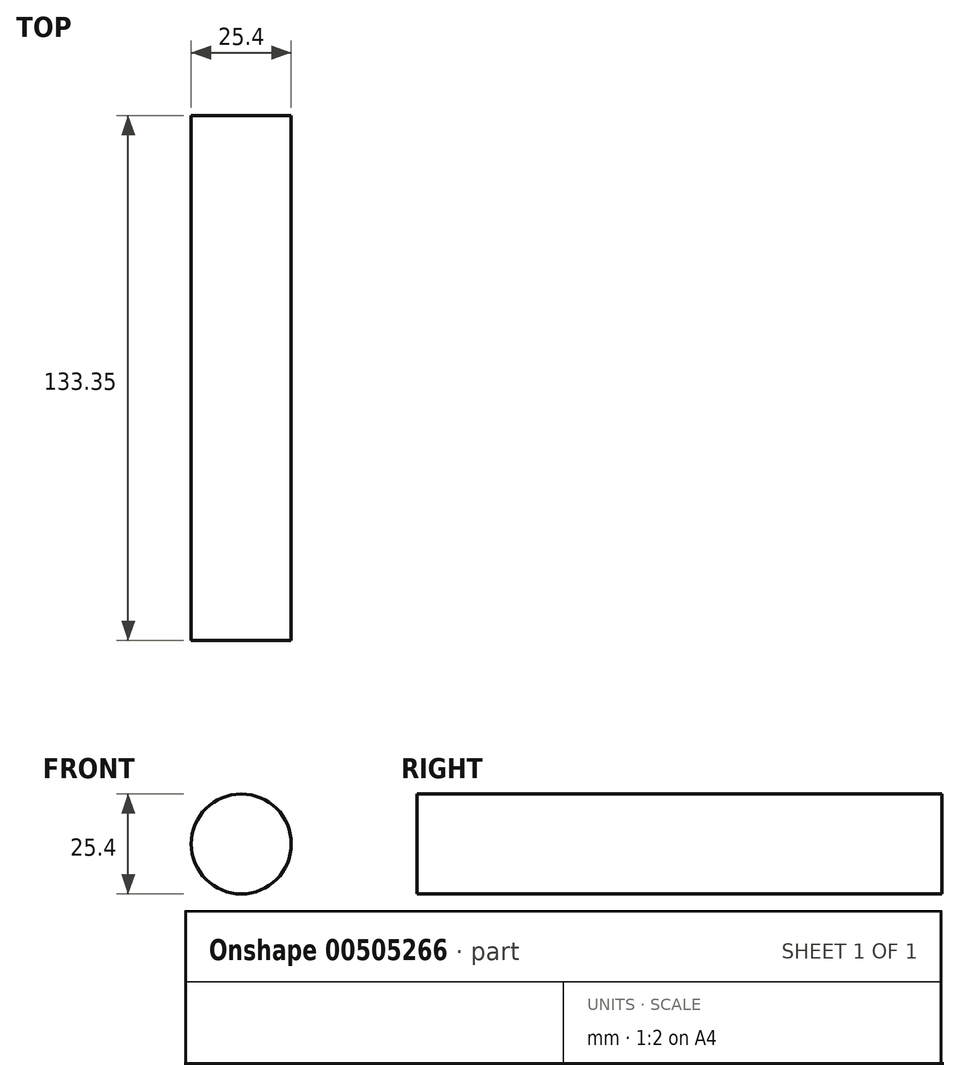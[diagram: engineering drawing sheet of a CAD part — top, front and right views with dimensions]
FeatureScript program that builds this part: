
annotation { "Feature Type Name" : "Feature", "Feature Type Description" : "" }
export const myFeature = defineFeature(function(context is Context, id is Id, definition is map)
    precondition{}
    {
        {
            var Q0;
            Q0=qCreatedBy(makeId("Front.planeOp"),FACE);
            var sketch = newSketch(context, id + "F0", { "sketchPlane" : qUnion([Q0])});
            skCircle(sketch, "E0", {"center": v(0, 0) * mm, "radius": 12.7 * mm});
            skSolve(sketch);
        }
        {
            var Q0;
            Q0=makeQuery(id+"F0.imprint","IMPRINT",FACE,{"disambiguationData":[TD([[makeQuery(id+"F0.imprint","IMPRINT",EDGE,{"derivedFrom":sQuery(id+"F0.wireOp",EDGE,"E0")}),1.0]])]});
            extrude(context, id + "F1", {"entities" : qUnion([Q0]), "depth" : 133.35 * mm});
        }
    });
